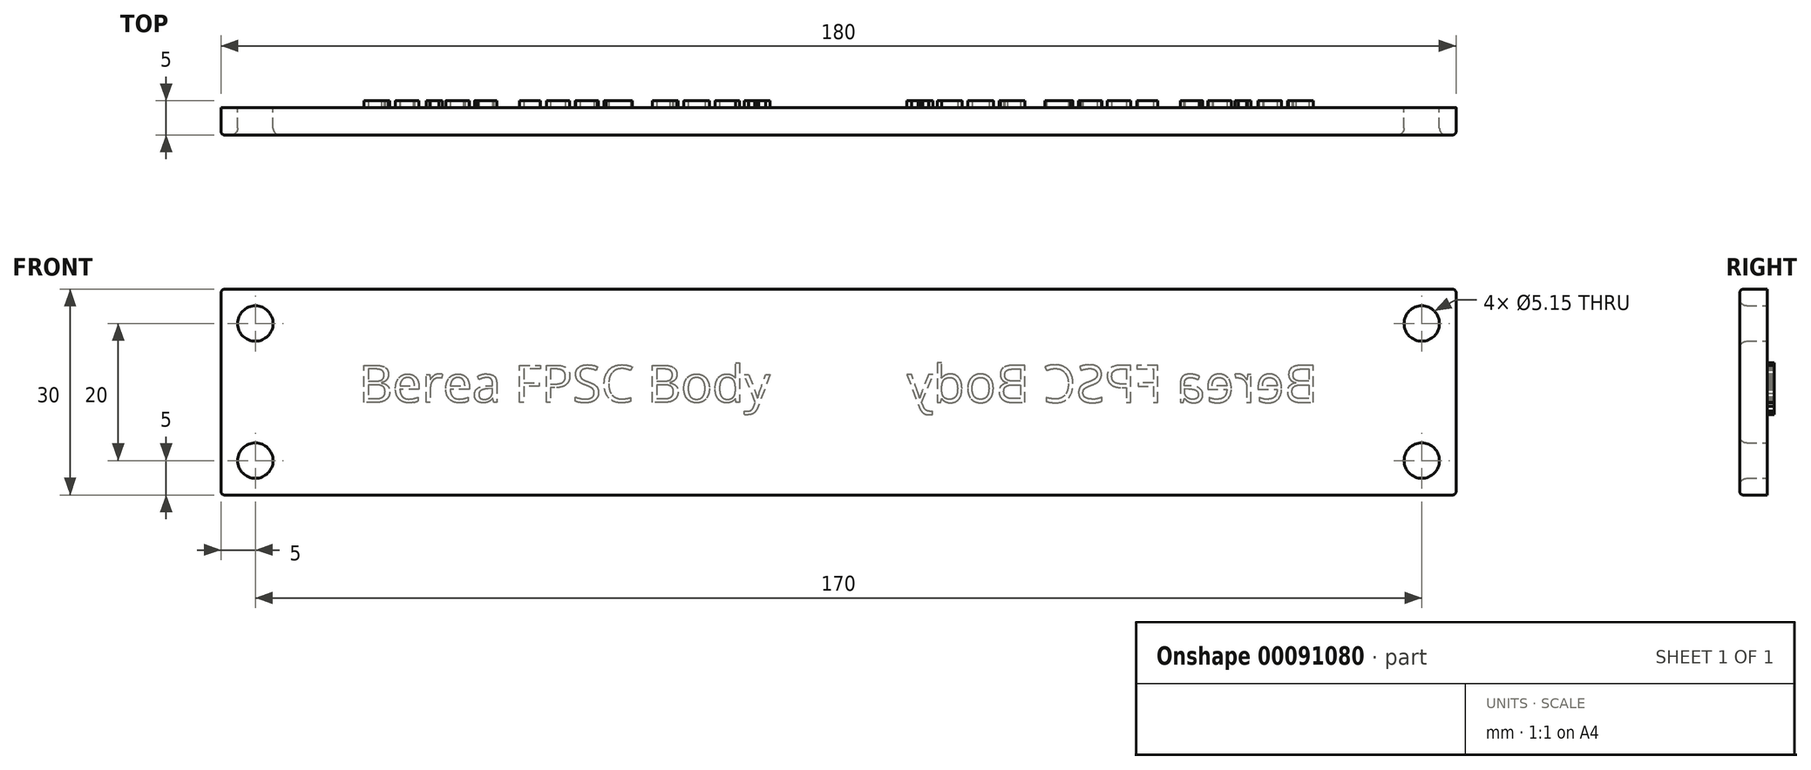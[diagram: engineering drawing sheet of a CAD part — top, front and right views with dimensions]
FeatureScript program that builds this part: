
annotation { "Feature Type Name" : "Feature", "Feature Type Description" : "" }
export const myFeature = defineFeature(function(context is Context, id is Id, definition is map)
    precondition{}
    {
        {
            var Q0;
            Q0=qCreatedBy(makeId("Front.planeOp"),FACE);
            var sketch = newSketch(context, id + "F0", { "sketchPlane" : qUnion([Q0])});
            skLineSegment(sketch, "E0.bottom", {"start": v(-90, -15) * mm, "end": v(90, -15) * mm});
            skLineSegment(sketch, "E0.top", {"start": v(-90, 15) * mm, "end": v(90, 15) * mm});
            skLineSegment(sketch, "E0.left", {"start": v(-90, -15) * mm, "end": v(-90, 15) * mm});
            skLineSegment(sketch, "E0.right", {"start": v(90, -15) * mm, "end": v(90, 15) * mm});
            skPoint(sketch, "E0.middle", {"position": v(0, 0) * mm});
            skCircle(sketch, "E1", {"center": v(-85, 10) * mm, "radius": 2.58 * mm});
            skPoint(sketch, "E2.start.orphan", {"position": v(-90, 0) * mm});
            skPoint(sketch, "E3.orphan", {"position": v(0, 15) * mm});
            skPoint(sketch, "E4.end.orphan", {"position": v(0, -15) * mm});
            skLineSegment(sketch, "E5", {"start": v(-90, 0) * mm, "end": v(0, 0) * mm, "construction": true});
            skLineSegment(sketch, "E6", {"start": v(0, 15) * mm, "end": v(0, -15) * mm, "construction": true});
            skCircle(sketch, "E7.MirrorC", {"center": v(-85, -10) * mm, "radius": 2.58 * mm});
            skCircle(sketch, "E8.MirrorC", {"center": v(85, 10) * mm, "radius": 2.58 * mm});
            skCircle(sketch, "E9.MirrorC", {"center": v(85, -10) * mm, "radius": 2.58 * mm});
            skSolve(sketch);
        }
        {
            var Q0;
            Q0=makeQuery(id+"F0.imprint","IMPRINT",FACE,{"disambiguationData":[TD([[makeQuery(id+"F0.imprint","IMPRINT",EDGE,{"derivedFrom":sQuery(id+"F0.wireOp",EDGE,"E0.bottom")}),1.0]])]});
            extrude(context, id + "F1", {"entities" : qUnion([Q0]), "depth" : 4 * mm});
        }
        {
            var Q0;
            Q0=makeQuery(id+"F1.opExtrude","CAP_EDGE",EDGE,{"disambiguationData":[OSD([sQuery(id+"F0.wireOp",EDGE,"E1")])],"isStart":false});
            var Q1;
            Q1=makeQuery(id+"F1.opExtrude","CAP_EDGE",EDGE,{"disambiguationData":[OSD([sQuery(id+"F0.wireOp",EDGE,"f5b72a5b-8583-449a-bdbf-9ac5a681e1fd0.MirrorC")])],"isStart":false});
            var Q2;
            Q2=makeQuery(id+"F1.opExtrude","CAP_EDGE",EDGE,{"disambiguationData":[OSD([sQuery(id+"F0.wireOp",EDGE,"2623e306-60f4-4522-aa65-1e3e8c2cf5b60.MirrorC")])],"isStart":false});
            var Q3;
            Q3=makeQuery(id+"F1.opExtrude","CAP_EDGE",EDGE,{"disambiguationData":[OSD([sQuery(id+"F0.wireOp",EDGE,"be81a34d-1d50-4ce7-a7a8-4484a1701fac0.MirrorC")])],"isStart":false});
            var Q4;
            Q4=makeQuery(id+"F1.opExtrude","CAP_EDGE",EDGE,{"disambiguationData":[OSD([sQuery(id+"F0.wireOp",EDGE,"E7.MirrorC")])],"isStart":false});
            var Q5;
            Q5=makeQuery(id+"F1.opExtrude","CAP_EDGE",EDGE,{"disambiguationData":[OSD([sQuery(id+"F0.wireOp",EDGE,"E8.MirrorC")])],"isStart":false});
            var Q6;
            Q6=makeQuery(id+"F1.opExtrude","CAP_EDGE",EDGE,{"disambiguationData":[OSD([sQuery(id+"F0.wireOp",EDGE,"E9.MirrorC")])],"isStart":false});
            fillet(context, id + "F2", {"entities" : qUnion([Q0, Q1, Q2, Q3, Q4, Q5, Q6]), "radius" : 1 * mm, "tangentPropagation" : true, "allowEdgeOverflow" : false});
        }
        {
            var Q0;
            Q0=makeQuery(id+"F1.opExtrude","CAP_EDGE",EDGE,{"disambiguationData":[OSD([sQuery(id+"F0.wireOp",EDGE,"E0.top")])],"isStart":false});
            var Q1;
            Q1=makeQuery(id+"F1.opExtrude","CAP_EDGE",EDGE,{"disambiguationData":[OSD([sQuery(id+"F0.wireOp",EDGE,"E0.left")])],"isStart":false});
            var Q2;
            Q2=makeQuery(id+"F1.opExtrude","CAP_EDGE",EDGE,{"disambiguationData":[OSD([sQuery(id+"F0.wireOp",EDGE,"E0.bottom")])],"isStart":false});
            var Q3;
            Q3=makeQuery(id+"F1.opExtrude","CAP_EDGE",EDGE,{"disambiguationData":[OSD([sQuery(id+"F0.wireOp",EDGE,"E0.right")])],"isStart":false});
            var Q4;
            Q4=makeQuery(id+"F1.opExtrude","SWEPT_EDGE",EDGE,{"disambiguationData":[OSD([sQuery(id+"F0.wireOp",EDGE,"E0.top"),sQuery(id+"F0.wireOp",EDGE,"E0.left")])]});
            var Q5;
            Q5=makeQuery(id+"F1.opExtrude","SWEPT_EDGE",EDGE,{"disambiguationData":[OSD([sQuery(id+"F0.wireOp",EDGE,"E0.bottom"),sQuery(id+"F0.wireOp",EDGE,"E0.left")])]});
            var Q6;
            Q6=makeQuery(id+"F1.opExtrude","SWEPT_EDGE",EDGE,{"disambiguationData":[OSD([sQuery(id+"F0.wireOp",EDGE,"E0.top"),sQuery(id+"F0.wireOp",EDGE,"E0.right")])]});
            var Q7;
            Q7=makeQuery(id+"F1.opExtrude","SWEPT_EDGE",EDGE,{"disambiguationData":[OSD([sQuery(id+"F0.wireOp",EDGE,"E0.bottom"),sQuery(id+"F0.wireOp",EDGE,"E0.right")])]});
            fillet(context, id + "F3", {"entities" : qUnion([Q0, Q1, Q2, Q3, Q4, Q5, Q6, Q7]), "radius" : .5 * mm, "tangentPropagation" : true, "allowEdgeOverflow" : false});
        }
        {
            var Q0;
            Q0=makeQuery(id+"F1.opExtrude","CAP_FACE",FACE,{"disambiguationData":[OSD([sQuery(id+"F0.wireOp",EDGE,"E0.bottom"),sQuery(id+"F0.wireOp",EDGE,"E0.top"),sQuery(id+"F0.wireOp",EDGE,"E0.left"),sQuery(id+"F0.wireOp",EDGE,"E0.right"),sQuery(id+"F0.wireOp",EDGE,"E1"),sQuery(id+"F0.wireOp",EDGE,"E7.MirrorC"),sQuery(id+"F0.wireOp",EDGE,"E8.MirrorC"),sQuery(id+"F0.wireOp",EDGE,"E9.MirrorC")])],"isStart":true});
            var sketch = newSketch(context, id + "F4", { "sketchPlane" : qUnion([Q0])});
            skText(sketch, "E10", { "text": "Berea FPSC Body", "fontName": "OpenSans-Regular.ttf"});
            skLineSegment(sketch, "E11", {"start": v(0, 15) * mm, "end": v(0, -15) * mm, "construction": true});
            const initialGuessF4  = {"E10": [-0.06991, -0.00149, 1, 0, 0.00545]};
            skSetInitialGuess(sketch, initialGuessF4);
            skSolve(sketch);
        }
        {
            var Q0;
            Q0=qSketchRegion(id+"F4",true);
            extrude(context, id + "F5", {"entities" : qUnion([Q0]), "operationType" : NewBodyOperationType.ADD, "depth" : 1 * mm});
        }
        {
            var Q0;
            Q0=makeQuery(id+"F1.opExtrude","SWEPT_BODY",BODY,{"disambiguationData":[OSD([sQuery(id+"F0.wireOp",EDGE,"E0.bottom"),sQuery(id+"F0.wireOp",EDGE,"E0.top"),sQuery(id+"F0.wireOp",EDGE,"E0.left"),sQuery(id+"F0.wireOp",EDGE,"E0.right"),sQuery(id+"F0.wireOp",EDGE,"E1"),sQuery(id+"F0.wireOp",EDGE,"E7.MirrorC"),sQuery(id+"F0.wireOp",EDGE,"E8.MirrorC"),sQuery(id+"F0.wireOp",EDGE,"E9.MirrorC")])]});
            var Q1;
            Q1=makeQuery(id+"F5.opExtrude","SWEPT_FACE",FACE,{"disambiguationData":[OSD([sQuery(id+"F4.wireOp",EDGE,"E10.sketch_text.stroke-94")])]});
            var Q2;
            Q2=makeQuery(id+"F5.opExtrude","SWEPT_FACE",FACE,{"disambiguationData":[OSD([sQuery(id+"F4.wireOp",EDGE,"E10.sketch_text.stroke-169")])]});
            var Q3;
            Q3=makeQuery(id+"F5.opExtrude","SWEPT_FACE",FACE,{"disambiguationData":[OSD([sQuery(id+"F4.wireOp",EDGE,"E10.sketch_text.stroke-185")])]});
            var Q4;
            Q4=makeQuery(id+"F5.opExtrude","SWEPT_FACE",FACE,{"disambiguationData":[OSD([sQuery(id+"F4.wireOp",EDGE,"E10.sketch_text.stroke-125")])]});
            var Q5;
            Q5=makeQuery(id+"F5.opExtrude","SWEPT_FACE",FACE,{"disambiguationData":[OSD([sQuery(id+"F4.wireOp",EDGE,"E10.sketch_text.stroke-155")])]});
            var Q6;
            Q6=makeQuery(id+"F5.opExtrude","SWEPT_FACE",FACE,{"disambiguationData":[OSD([sQuery(id+"F4.wireOp",EDGE,"E10.sketch_text.stroke-65")])]});
            var Q7;
            Q7=makeQuery(id+"F5.opExtrude","SWEPT_FACE",FACE,{"disambiguationData":[OSD([sQuery(id+"F4.wireOp",EDGE,"E10.sketch_text.stroke-81")])]});
            var Q8;
            Q8=makeQuery(id+"F5.opExtrude","SWEPT_FACE",FACE,{"disambiguationData":[OSD([sQuery(id+"F4.wireOp",EDGE,"E10.sketch_text.stroke-67")])]});
            var Q9;
            Q9=makeQuery(id+"F5.opExtrude","SWEPT_FACE",FACE,{"disambiguationData":[OSD([sQuery(id+"F4.wireOp",EDGE,"E10.sketch_text.stroke-99")])]});
            var Q10;
            Q10=makeQuery(id+"F5.opExtrude","SWEPT_FACE",FACE,{"disambiguationData":[OSD([sQuery(id+"F4.wireOp",EDGE,"E10.sketch_text.stroke-127")])]});
            var Q11;
            Q11=makeQuery(id+"F5.opExtrude","SWEPT_FACE",FACE,{"disambiguationData":[OSD([sQuery(id+"F4.wireOp",EDGE,"E10.sketch_text.stroke-10")])]});
            var Q12;
            Q12=makeQuery(id+"F5.opExtrude","CAP_FACE",FACE,{"disambiguationData":[OSD([sQuery(id+"F4.wireOp",EDGE,"E10.sketch_text.stroke-9"),sQuery(id+"F4.wireOp",EDGE,"E10.sketch_text.stroke-10"),sQuery(id+"F4.wireOp",EDGE,"E10.sketch_text.stroke-11"),sQuery(id+"F4.wireOp",EDGE,"E10.sketch_text.stroke-12")])],"isStart":false});
            var Q13;
            Q13=makeQuery(id+"F5.opExtrude","SWEPT_FACE",FACE,{"disambiguationData":[OSD([sQuery(id+"F4.wireOp",EDGE,"E10.sketch_text.stroke-154")])]});
            var Q14;
            Q14=makeQuery(id+"F5.opExtrude","SWEPT_FACE",FACE,{"disambiguationData":[OSD([sQuery(id+"F4.wireOp",EDGE,"E10.sketch_text.stroke-1")])]});
            var Q15;
            Q15=makeQuery(id+"F5.opExtrude","CAP_FACE",FACE,{"disambiguationData":[OSD([sQuery(id+"F4.wireOp",EDGE,"E10.sketch_text.stroke-124"),sQuery(id+"F4.wireOp",EDGE,"E10.sketch_text.stroke-125"),sQuery(id+"F4.wireOp",EDGE,"E10.sketch_text.stroke-126"),sQuery(id+"F4.wireOp",EDGE,"E10.sketch_text.stroke-127"),sQuery(id+"F4.wireOp",EDGE,"E10.sketch_text.stroke-128"),sQuery(id+"F4.wireOp",EDGE,"E10.sketch_text.stroke-129"),sQuery(id+"F4.wireOp",EDGE,"E10.sketch_text.stroke-130"),sQuery(id+"F4.wireOp",EDGE,"E10.sketch_text.stroke-131"),sQuery(id+"F4.wireOp",EDGE,"E10.sketch_text.stroke-132"),sQuery(id+"F4.wireOp",EDGE,"E10.sketch_text.stroke-133"),sQuery(id+"F4.wireOp",EDGE,"E10.sketch_text.stroke-134"),sQuery(id+"F4.wireOp",EDGE,"E10.sketch_text.stroke-135"),sQuery(id+"F4.wireOp",EDGE,"E10.sketch_text.stroke-136"),sQuery(id+"F4.wireOp",EDGE,"E10.sketch_text.stroke-137"),sQuery(id+"F4.wireOp",EDGE,"E10.sketch_text.stroke-138")])],"isStart":false});
            var Q16;
            Q16=makeQuery(id+"F5.opExtrude","CAP_FACE",FACE,{"disambiguationData":[OSD([sQuery(id+"F4.wireOp",EDGE,"E10.sketch_text.stroke-34"),sQuery(id+"F4.wireOp",EDGE,"E10.sketch_text.stroke-35"),sQuery(id+"F4.wireOp",EDGE,"E10.sketch_text.stroke-36"),sQuery(id+"F4.wireOp",EDGE,"E10.sketch_text.stroke-37"),sQuery(id+"F4.wireOp",EDGE,"E10.sketch_text.stroke-38"),sQuery(id+"F4.wireOp",EDGE,"E10.sketch_text.stroke-39"),sQuery(id+"F4.wireOp",EDGE,"E10.sketch_text.stroke-40"),sQuery(id+"F4.wireOp",EDGE,"E10.sketch_text.stroke-41"),sQuery(id+"F4.wireOp",EDGE,"E10.sketch_text.stroke-42"),sQuery(id+"F4.wireOp",EDGE,"E10.sketch_text.stroke-43"),sQuery(id+"F4.wireOp",EDGE,"E10.sketch_text.stroke-44"),sQuery(id+"F4.wireOp",EDGE,"E10.sketch_text.stroke-45"),sQuery(id+"F4.wireOp",EDGE,"E10.sketch_text.stroke-46"),sQuery(id+"F4.wireOp",EDGE,"E10.sketch_text.stroke-47"),sQuery(id+"F4.wireOp",EDGE,"E10.sketch_text.stroke-48"),sQuery(id+"F4.wireOp",EDGE,"E10.sketch_text.stroke-49"),sQuery(id+"F4.wireOp",EDGE,"E10.sketch_text.stroke-50"),sQuery(id+"F4.wireOp",EDGE,"E10.sketch_text.stroke-51"),sQuery(id+"F4.wireOp",EDGE,"E10.sketch_text.stroke-52"),sQuery(id+"F4.wireOp",EDGE,"E10.sketch_text.stroke-53"),sQuery(id+"F4.wireOp",EDGE,"E10.sketch_text.stroke-54"),sQuery(id+"F4.wireOp",EDGE,"E10.sketch_text.stroke-55"),sQuery(id+"F4.wireOp",EDGE,"E10.sketch_text.stroke-56"),sQuery(id+"F4.wireOp",EDGE,"E10.sketch_text.stroke-57"),sQuery(id+"F4.wireOp",EDGE,"E10.sketch_text.stroke-58"),sQuery(id+"F4.wireOp",EDGE,"E10.sketch_text.stroke-59"),sQuery(id+"F4.wireOp",EDGE,"E10.sketch_text.stroke-60")])],"isStart":false});
            var Q17;
            Q17=makeQuery(id+"F5.opExtrude","SWEPT_FACE",FACE,{"disambiguationData":[OSD([sQuery(id+"F4.wireOp",EDGE,"E10.sketch_text.stroke-50")])]});
            var Q18;
            Q18=makeQuery(id+"F5.opExtrude","SWEPT_FACE",FACE,{"disambiguationData":[OSD([sQuery(id+"F4.wireOp",EDGE,"E10.sketch_text.stroke-2")])]});
            var Q19;
            Q19=makeQuery(id+"F5.opExtrude","SWEPT_FACE",FACE,{"disambiguationData":[OSD([sQuery(id+"F4.wireOp",EDGE,"E10.sketch_text.stroke-3")])]});
            var Q20;
            Q20=makeQuery(id+"F5.opExtrude","SWEPT_FACE",FACE,{"disambiguationData":[OSD([sQuery(id+"F4.wireOp",EDGE,"E10.sketch_text.stroke-5")])]});
            var Q21;
            Q21=makeQuery(id+"F5.opExtrude","SWEPT_FACE",FACE,{"disambiguationData":[OSD([sQuery(id+"F4.wireOp",EDGE,"E10.sketch_text.stroke-8")])]});
            var Q22;
            Q22=makeQuery(id+"F5.opExtrude","SWEPT_FACE",FACE,{"disambiguationData":[OSD([sQuery(id+"F4.wireOp",EDGE,"E10.sketch_text.stroke-98")])]});
            var Q23;
            Q23=makeQuery(id+"F5.opExtrude","SWEPT_FACE",FACE,{"disambiguationData":[OSD([sQuery(id+"F4.wireOp",EDGE,"E10.sketch_text.stroke-66")])]});
            var Q24;
            Q24=makeQuery(id+"F5.opExtrude","SWEPT_FACE",FACE,{"disambiguationData":[OSD([sQuery(id+"F4.wireOp",EDGE,"E10.sketch_text.stroke-153")])]});
            var Q25;
            Q25=makeQuery(id+"F5.opExtrude","SWEPT_FACE",FACE,{"disambiguationData":[OSD([sQuery(id+"F4.wireOp",EDGE,"E10.sketch_text.stroke-126")])]});
            var Q26;
            Q26=makeQuery(id+"F5.opExtrude","SWEPT_FACE",FACE,{"disambiguationData":[OSD([sQuery(id+"F4.wireOp",EDGE,"E10.sketch_text.stroke-183")])]});
            var Q27;
            Q27=makeQuery(id+"F5.opExtrude","SWEPT_FACE",FACE,{"disambiguationData":[OSD([sQuery(id+"F4.wireOp",EDGE,"E10.sketch_text.stroke-109")])]});
            var Q28;
            Q28=makeQuery(id+"F5.opExtrude","SWEPT_FACE",FACE,{"disambiguationData":[OSD([sQuery(id+"F4.wireOp",EDGE,"E10.sketch_text.stroke-186")])]});
            var Q29;
            Q29=makeQuery(id+"F5.opExtrude","SWEPT_FACE",FACE,{"disambiguationData":[OSD([sQuery(id+"F4.wireOp",EDGE,"E10.sketch_text.stroke-79")])]});
            var Q30;
            Q30=makeQuery(id+"F5.opExtrude","SWEPT_FACE",FACE,{"disambiguationData":[OSD([sQuery(id+"F4.wireOp",EDGE,"E10.sketch_text.stroke-110")])]});
            var Q31;
            Q31=makeQuery(id+"F5.opExtrude","SWEPT_FACE",FACE,{"disambiguationData":[OSD([sQuery(id+"F4.wireOp",EDGE,"E10.sketch_text.stroke-38")])]});
            var Q32;
            Q32=makeQuery(id+"F5.opExtrude","SWEPT_FACE",FACE,{"disambiguationData":[OSD([sQuery(id+"F4.wireOp",EDGE,"E10.sketch_text.stroke-24")])]});
            var Q33;
            Q33=makeQuery(id+"F5.opExtrude","SWEPT_FACE",FACE,{"disambiguationData":[OSD([sQuery(id+"F4.wireOp",EDGE,"E10.sketch_text.stroke-12")])]});
            var Q34;
            Q34=makeQuery(id+"F5.opExtrude","SWEPT_FACE",FACE,{"disambiguationData":[OSD([sQuery(id+"F4.wireOp",EDGE,"E10.sketch_text.stroke-100")])]});
            var Q35;
            Q35=makeQuery(id+"F5.opExtrude","SWEPT_FACE",FACE,{"disambiguationData":[OSD([sQuery(id+"F4.wireOp",EDGE,"E10.sketch_text.stroke-158")])]});
            var Q36;
            Q36=makeQuery(id+"F5.opExtrude","SWEPT_FACE",FACE,{"disambiguationData":[OSD([sQuery(id+"F4.wireOp",EDGE,"E10.sketch_text.stroke-142")])]});
            var Q37;
            Q37=makeQuery(id+"F5.opExtrude","SWEPT_FACE",FACE,{"disambiguationData":[OSD([sQuery(id+"F4.wireOp",EDGE,"E10.sketch_text.stroke-54")])]});
            var Q38;
            Q38=makeQuery(id+"F5.opExtrude","SWEPT_FACE",FACE,{"disambiguationData":[OSD([sQuery(id+"F4.wireOp",EDGE,"E10.sketch_text.stroke-25")])]});
            var Q39;
            Q39=makeQuery(id+"F5.opExtrude","SWEPT_FACE",FACE,{"disambiguationData":[OSD([sQuery(id+"F4.wireOp",EDGE,"E10.sketch_text.stroke-101")])]});
            var Q40;
            Q40=makeQuery(id+"F5.opExtrude","SWEPT_FACE",FACE,{"disambiguationData":[OSD([sQuery(id+"F4.wireOp",EDGE,"E10.sketch_text.stroke-69")])]});
            var Q41;
            Q41=makeQuery(id+"F5.opExtrude","SWEPT_FACE",FACE,{"disambiguationData":[OSD([sQuery(id+"F4.wireOp",EDGE,"E10.sketch_text.stroke-159")])]});
            var Q42;
            Q42=makeQuery(id+"F5.opExtrude","SWEPT_FACE",FACE,{"disambiguationData":[OSD([sQuery(id+"F4.wireOp",EDGE,"E10.sketch_text.stroke-85")])]});
            var Q43;
            Q43=makeQuery(id+"F5.opExtrude","SWEPT_FACE",FACE,{"disambiguationData":[OSD([sQuery(id+"F4.wireOp",EDGE,"E10.sketch_text.stroke-173")])]});
            var Q44;
            Q44=makeQuery(id+"F5.opExtrude","SWEPT_FACE",FACE,{"disambiguationData":[OSD([sQuery(id+"F4.wireOp",EDGE,"E10.sketch_text.stroke-40")])]});
            var Q45;
            Q45=makeQuery(id+"F5.opExtrude","SWEPT_FACE",FACE,{"disambiguationData":[OSD([sQuery(id+"F4.wireOp",EDGE,"E10.sketch_text.stroke-102")])]});
            var Q46;
            Q46=makeQuery(id+"F5.opExtrude","SWEPT_FACE",FACE,{"disambiguationData":[OSD([sQuery(id+"F4.wireOp",EDGE,"E10.sketch_text.stroke-86")])]});
            var Q47;
            Q47=makeQuery(id+"F5.opExtrude","SWEPT_FACE",FACE,{"disambiguationData":[OSD([sQuery(id+"F4.wireOp",EDGE,"E10.sketch_text.stroke-130")])]});
            var Q48;
            Q48=makeQuery(id+"F5.opExtrude","SWEPT_FACE",FACE,{"disambiguationData":[OSD([sQuery(id+"F4.wireOp",EDGE,"E10.sketch_text.stroke-103")])]});
            var Q49;
            Q49=makeQuery(id+"F5.opExtrude","SWEPT_FACE",FACE,{"disambiguationData":[OSD([sQuery(id+"F4.wireOp",EDGE,"E10.sketch_text.stroke-87")])]});
            var Q50;
            Q50=makeQuery(id+"F5.opExtrude","SWEPT_FACE",FACE,{"disambiguationData":[OSD([sQuery(id+"F4.wireOp",EDGE,"E10.sketch_text.stroke-145")])]});
            var Q51;
            Q51=makeQuery(id+"F5.opExtrude","SWEPT_FACE",FACE,{"disambiguationData":[OSD([sQuery(id+"F4.wireOp",EDGE,"E10.sketch_text.stroke-131")])]});
            var Q52;
            Q52=makeQuery(id+"F5.opExtrude","SWEPT_FACE",FACE,{"disambiguationData":[OSD([sQuery(id+"F4.wireOp",EDGE,"E10.sketch_text.stroke-28")])]});
            var Q53;
            Q53=makeQuery(id+"F5.opExtrude","SWEPT_FACE",FACE,{"disambiguationData":[OSD([sQuery(id+"F4.wireOp",EDGE,"E10.sketch_text.stroke-14")])]});
            var Q54;
            Q54=makeQuery(id+"F5.opExtrude","SWEPT_FACE",FACE,{"disambiguationData":[OSD([sQuery(id+"F4.wireOp",EDGE,"E10.sketch_text.stroke-88")])]});
            var Q55;
            Q55=makeQuery(id+"F5.opExtrude","SWEPT_FACE",FACE,{"disambiguationData":[OSD([sQuery(id+"F4.wireOp",EDGE,"E10.sketch_text.stroke-162")])]});
            var Q56;
            Q56=makeQuery(id+"F5.opExtrude","SWEPT_FACE",FACE,{"disambiguationData":[OSD([sQuery(id+"F4.wireOp",EDGE,"E10.sketch_text.stroke-176")])]});
            var Q57;
            Q57=makeQuery(id+"F5.opExtrude","SWEPT_FACE",FACE,{"disambiguationData":[OSD([sQuery(id+"F4.wireOp",EDGE,"E10.sketch_text.stroke-73")])]});
            var Q58;
            Q58=makeQuery(id+"F5.opExtrude","SWEPT_FACE",FACE,{"disambiguationData":[OSD([sQuery(id+"F4.wireOp",EDGE,"E10.sketch_text.stroke-59")])]});
            var Q59;
            Q59=makeQuery(id+"F5.opExtrude","SWEPT_FACE",FACE,{"disambiguationData":[OSD([sQuery(id+"F4.wireOp",EDGE,"E10.sketch_text.stroke-133")])]});
            var Q60;
            Q60=makeQuery(id+"F5.opExtrude","SWEPT_FACE",FACE,{"disambiguationData":[OSD([sQuery(id+"F4.wireOp",EDGE,"E10.sketch_text.stroke-119")])]});
            var Q61;
            Q61=makeQuery(id+"F5.opExtrude","SWEPT_FACE",FACE,{"disambiguationData":[OSD([sQuery(id+"F4.wireOp",EDGE,"E10.sketch_text.stroke-74")])]});
            var Q62;
            Q62=makeQuery(id+"F5.opExtrude","SWEPT_FACE",FACE,{"disambiguationData":[OSD([sQuery(id+"F4.wireOp",EDGE,"E10.sketch_text.stroke-44")])]});
            var Q63;
            Q63=makeQuery(id+"F5.opExtrude","SWEPT_FACE",FACE,{"disambiguationData":[OSD([sQuery(id+"F4.wireOp",EDGE,"E10.sketch_text.stroke-120")])]});
            var Q64;
            Q64=makeQuery(id+"F5.opExtrude","SWEPT_FACE",FACE,{"disambiguationData":[OSD([sQuery(id+"F4.wireOp",EDGE,"E10.sketch_text.stroke-90")])]});
            var Q65;
            Q65=makeQuery(id+"F5.opExtrude","SWEPT_FACE",FACE,{"disambiguationData":[OSD([sQuery(id+"F4.wireOp",EDGE,"E10.sketch_text.stroke-178")])]});
            var Q66;
            Q66=makeQuery(id+"F5.opExtrude","SWEPT_FACE",FACE,{"disambiguationData":[OSD([sQuery(id+"F4.wireOp",EDGE,"E10.sketch_text.stroke-45")])]});
            var Q67;
            Q67=makeQuery(id+"F5.opExtrude","SWEPT_FACE",FACE,{"disambiguationData":[OSD([sQuery(id+"F4.wireOp",EDGE,"E10.sketch_text.stroke-31")])]});
            var Q68;
            Q68=makeQuery(id+"F5.opExtrude","SWEPT_FACE",FACE,{"disambiguationData":[OSD([sQuery(id+"F4.wireOp",EDGE,"E10.sketch_text.stroke-135")])]});
            var Q69;
            Q69=makeQuery(id+"F5.opExtrude","SWEPT_FACE",FACE,{"disambiguationData":[OSD([sQuery(id+"F4.wireOp",EDGE,"E10.sketch_text.stroke-179")])]});
            var Q70;
            Q70=makeQuery(id+"F5.opExtrude","SWEPT_FACE",FACE,{"disambiguationData":[OSD([sQuery(id+"F4.wireOp",EDGE,"E10.sketch_text.stroke-165")])]});
            var Q71;
            Q71=makeQuery(id+"F5.opExtrude","SWEPT_FACE",FACE,{"disambiguationData":[OSD([sQuery(id+"F4.wireOp",EDGE,"E10.sketch_text.stroke-149")])]});
            var Q72;
            Q72=makeQuery(id+"F5.opExtrude","SWEPT_FACE",FACE,{"disambiguationData":[OSD([sQuery(id+"F4.wireOp",EDGE,"E10.sketch_text.stroke-136")])]});
            var Q73;
            Q73=makeQuery(id+"F5.opExtrude","SWEPT_FACE",FACE,{"disambiguationData":[OSD([sQuery(id+"F4.wireOp",EDGE,"E10.sketch_text.stroke-122")])]});
            var Q74;
            Q74=makeQuery(id+"F5.opExtrude","SWEPT_FACE",FACE,{"disambiguationData":[OSD([sQuery(id+"F4.wireOp",EDGE,"E10.sketch_text.stroke-106")])]});
            var Q75;
            Q75=makeQuery(id+"F5.opExtrude","SWEPT_FACE",FACE,{"disambiguationData":[OSD([sQuery(id+"F4.wireOp",EDGE,"E10.sketch_text.stroke-180")])]});
            var Q76;
            Q76=makeQuery(id+"F5.opExtrude","SWEPT_FACE",FACE,{"disambiguationData":[OSD([sQuery(id+"F4.wireOp",EDGE,"E10.sketch_text.stroke-166")])]});
            var Q77;
            Q77=makeQuery(id+"F5.opExtrude","SWEPT_FACE",FACE,{"disambiguationData":[OSD([sQuery(id+"F4.wireOp",EDGE,"E10.sketch_text.stroke-150")])]});
            var Q78;
            Q78=makeQuery(id+"F5.opExtrude","SWEPT_FACE",FACE,{"disambiguationData":[OSD([sQuery(id+"F4.wireOp",EDGE,"E10.sketch_text.stroke-76")])]});
            var Q79;
            Q79=makeQuery(id+"F5.opExtrude","SWEPT_FACE",FACE,{"disambiguationData":[OSD([sQuery(id+"F4.wireOp",EDGE,"E10.sketch_text.stroke-32")])]});
            var Q80;
            Q80=makeQuery(id+"F5.opExtrude","SWEPT_FACE",FACE,{"disambiguationData":[OSD([sQuery(id+"F4.wireOp",EDGE,"E10.sketch_text.stroke-181")])]});
            var Q81;
            Q81=makeQuery(id+"F5.opExtrude","SWEPT_FACE",FACE,{"disambiguationData":[OSD([sQuery(id+"F4.wireOp",EDGE,"E10.sketch_text.stroke-47")])]});
            var Q82;
            Q82=makeQuery(id+"F5.opExtrude","SWEPT_FACE",FACE,{"disambiguationData":[OSD([sQuery(id+"F4.wireOp",EDGE,"E10.sketch_text.stroke-123")])]});
            var Q83;
            Q83=makeQuery(id+"F5.opExtrude","SWEPT_FACE",FACE,{"disambiguationData":[OSD([sQuery(id+"F4.wireOp",EDGE,"E10.sketch_text.stroke-107")])]});
            var Q84;
            Q84=makeQuery(id+"F5.opExtrude","SWEPT_FACE",FACE,{"disambiguationData":[OSD([sQuery(id+"F4.wireOp",EDGE,"E10.sketch_text.stroke-48")])]});
            var Q85;
            Q85=makeQuery(id+"F5.opExtrude","SWEPT_FACE",FACE,{"disambiguationData":[OSD([sQuery(id+"F4.wireOp",EDGE,"E10.sketch_text.stroke-124")])]});
            var Q86;
            Q86=makeQuery(id+"F5.opExtrude","SWEPT_FACE",FACE,{"disambiguationData":[OSD([sQuery(id+"F4.wireOp",EDGE,"E10.sketch_text.stroke-108")])]});
            var Q87;
            Q87=makeQuery(id+"F5.opExtrude","CAP_FACE",FACE,{"disambiguationData":[OSD([sQuery(id+"F4.wireOp",EDGE,"E10.sketch_text.stroke-139"),sQuery(id+"F4.wireOp",EDGE,"E10.sketch_text.stroke-140"),sQuery(id+"F4.wireOp",EDGE,"E10.sketch_text.stroke-141"),sQuery(id+"F4.wireOp",EDGE,"E10.sketch_text.stroke-142"),sQuery(id+"F4.wireOp",EDGE,"E10.sketch_text.stroke-143"),sQuery(id+"F4.wireOp",EDGE,"E10.sketch_text.stroke-144"),sQuery(id+"F4.wireOp",EDGE,"E10.sketch_text.stroke-145"),sQuery(id+"F4.wireOp",EDGE,"E10.sketch_text.stroke-146"),sQuery(id+"F4.wireOp",EDGE,"E10.sketch_text.stroke-147"),sQuery(id+"F4.wireOp",EDGE,"E10.sketch_text.stroke-148"),sQuery(id+"F4.wireOp",EDGE,"E10.sketch_text.stroke-149"),sQuery(id+"F4.wireOp",EDGE,"E10.sketch_text.stroke-150"),sQuery(id+"F4.wireOp",EDGE,"E10.sketch_text.stroke-151"),sQuery(id+"F4.wireOp",EDGE,"E10.sketch_text.stroke-152"),sQuery(id+"F4.wireOp",EDGE,"E10.sketch_text.stroke-153"),sQuery(id+"F4.wireOp",EDGE,"E10.sketch_text.stroke-154"),sQuery(id+"F4.wireOp",EDGE,"E10.sketch_text.stroke-155"),sQuery(id+"F4.wireOp",EDGE,"E10.sketch_text.stroke-156"),sQuery(id+"F4.wireOp",EDGE,"E10.sketch_text.stroke-157"),sQuery(id+"F4.wireOp",EDGE,"E10.sketch_text.stroke-158"),sQuery(id+"F4.wireOp",EDGE,"E10.sketch_text.stroke-159"),sQuery(id+"F4.wireOp",EDGE,"E10.sketch_text.stroke-160"),sQuery(id+"F4.wireOp",EDGE,"E10.sketch_text.stroke-161"),sQuery(id+"F4.wireOp",EDGE,"E10.sketch_text.stroke-162"),sQuery(id+"F4.wireOp",EDGE,"E10.sketch_text.stroke-163"),sQuery(id+"F4.wireOp",EDGE,"E10.sketch_text.stroke-164"),sQuery(id+"F4.wireOp",EDGE,"E10.sketch_text.stroke-165")])],"isStart":false});
            var Q88;
            Q88=makeQuery(id+"F5.opExtrude","CAP_FACE",FACE,{"disambiguationData":[OSD([sQuery(id+"F4.wireOp",EDGE,"E10.sketch_text.stroke-21"),sQuery(id+"F4.wireOp",EDGE,"E10.sketch_text.stroke-22"),sQuery(id+"F4.wireOp",EDGE,"E10.sketch_text.stroke-23"),sQuery(id+"F4.wireOp",EDGE,"E10.sketch_text.stroke-24"),sQuery(id+"F4.wireOp",EDGE,"E10.sketch_text.stroke-25"),sQuery(id+"F4.wireOp",EDGE,"E10.sketch_text.stroke-26"),sQuery(id+"F4.wireOp",EDGE,"E10.sketch_text.stroke-27"),sQuery(id+"F4.wireOp",EDGE,"E10.sketch_text.stroke-28"),sQuery(id+"F4.wireOp",EDGE,"E10.sketch_text.stroke-29"),sQuery(id+"F4.wireOp",EDGE,"E10.sketch_text.stroke-30"),sQuery(id+"F4.wireOp",EDGE,"E10.sketch_text.stroke-31"),sQuery(id+"F4.wireOp",EDGE,"E10.sketch_text.stroke-32"),sQuery(id+"F4.wireOp",EDGE,"E10.sketch_text.stroke-33")])],"isStart":false});
            var Q89;
            Q89=makeQuery(id+"F5.opExtrude","SWEPT_FACE",FACE,{"disambiguationData":[OSD([sQuery(id+"F4.wireOp",EDGE,"E10.sketch_text.stroke-113")])]});
            var Q90;
            Q90=makeQuery(id+"F5.opExtrude","SWEPT_FACE",FACE,{"disambiguationData":[OSD([sQuery(id+"F4.wireOp",EDGE,"E10.sketch_text.stroke-37")])]});
            var Q91;
            Q91=makeQuery(id+"F5.opExtrude","SWEPT_FACE",FACE,{"disambiguationData":[OSD([sQuery(id+"F4.wireOp",EDGE,"E10.sketch_text.stroke-187")])]});
            var Q92;
            Q92=makeQuery(id+"F5.opExtrude","SWEPT_FACE",FACE,{"disambiguationData":[OSD([sQuery(id+"F4.wireOp",EDGE,"E10.sketch_text.stroke-0")])]});
            var Q93;
            Q93=makeQuery(id+"F5.opExtrude","SWEPT_FACE",FACE,{"disambiguationData":[OSD([sQuery(id+"F4.wireOp",EDGE,"E10.sketch_text.stroke-4")])]});
            var Q94;
            Q94=makeQuery(id+"F5.opExtrude","SWEPT_FACE",FACE,{"disambiguationData":[OSD([sQuery(id+"F4.wireOp",EDGE,"E10.sketch_text.stroke-82")])]});
            var Q95;
            Q95=makeQuery(id+"F5.opExtrude","SWEPT_FACE",FACE,{"disambiguationData":[OSD([sQuery(id+"F4.wireOp",EDGE,"E10.sketch_text.stroke-52")])]});
            var Q96;
            Q96=makeQuery(id+"F5.opExtrude","SWEPT_FACE",FACE,{"disambiguationData":[OSD([sQuery(id+"F4.wireOp",EDGE,"E10.sketch_text.stroke-49")])]});
            var Q97;
            Q97=makeQuery(id+"F5.opExtrude","SWEPT_FACE",FACE,{"disambiguationData":[OSD([sQuery(id+"F4.wireOp",EDGE,"E10.sketch_text.stroke-63")])]});
            var Q98;
            Q98=makeQuery(id+"F5.opExtrude","SWEPT_FACE",FACE,{"disambiguationData":[OSD([sQuery(id+"F4.wireOp",EDGE,"E10.sketch_text.stroke-21")])]});
            var Q99;
            Q99=makeQuery(id+"F5.opExtrude","SWEPT_FACE",FACE,{"disambiguationData":[OSD([sQuery(id+"F4.wireOp",EDGE,"E10.sketch_text.stroke-128")])]});
            var Q100;
            Q100=makeQuery(id+"F5.opExtrude","SWEPT_FACE",FACE,{"disambiguationData":[OSD([sQuery(id+"F4.wireOp",EDGE,"E10.sketch_text.stroke-55")])]});
            var Q101;
            Q101=makeQuery(id+"F5.opExtrude","SWEPT_FACE",FACE,{"disambiguationData":[OSD([sQuery(id+"F4.wireOp",EDGE,"E10.sketch_text.stroke-26")])]});
            var Q102;
            Q102=makeQuery(id+"F5.opExtrude","SWEPT_FACE",FACE,{"disambiguationData":[OSD([sQuery(id+"F4.wireOp",EDGE,"E10.sketch_text.stroke-174")])]});
            var Q103;
            Q103=makeQuery(id+"F5.opExtrude","SWEPT_FACE",FACE,{"disambiguationData":[OSD([sQuery(id+"F4.wireOp",EDGE,"E10.sketch_text.stroke-104")])]});
            var Q104;
            Q104=makeQuery(id+"F5.opExtrude","SWEPT_FACE",FACE,{"disambiguationData":[OSD([sQuery(id+"F4.wireOp",EDGE,"E10.sketch_text.stroke-72")])]});
            var Q105;
            Q105=makeQuery(id+"F5.opExtrude","SWEPT_FACE",FACE,{"disambiguationData":[OSD([sQuery(id+"F4.wireOp",EDGE,"E10.sketch_text.stroke-132")])]});
            var Q106;
            Q106=makeQuery(id+"F5.opExtrude","SWEPT_FACE",FACE,{"disambiguationData":[OSD([sQuery(id+"F4.wireOp",EDGE,"E10.sketch_text.stroke-43")])]});
            var Q107;
            Q107=makeQuery(id+"F5.opExtrude","SWEPT_FACE",FACE,{"disambiguationData":[OSD([sQuery(id+"F4.wireOp",EDGE,"E10.sketch_text.stroke-15")])]});
            var Q108;
            Q108=makeQuery(id+"F5.opExtrude","SWEPT_FACE",FACE,{"disambiguationData":[OSD([sQuery(id+"F4.wireOp",EDGE,"E10.sketch_text.stroke-89")])]});
            var Q109;
            Q109=makeQuery(id+"F5.opExtrude","SWEPT_FACE",FACE,{"disambiguationData":[OSD([sQuery(id+"F4.wireOp",EDGE,"E10.sketch_text.stroke-163")])]});
            var Q110;
            Q110=makeQuery(id+"F5.opExtrude","SWEPT_FACE",FACE,{"disambiguationData":[OSD([sQuery(id+"F4.wireOp",EDGE,"E10.sketch_text.stroke-30")])]});
            var Q111;
            Q111=makeQuery(id+"F5.opExtrude","SWEPT_FACE",FACE,{"disambiguationData":[OSD([sQuery(id+"F4.wireOp",EDGE,"E10.sketch_text.stroke-134")])]});
            var Q112;
            Q112=makeQuery(id+"F5.opExtrude","SWEPT_FACE",FACE,{"disambiguationData":[OSD([sQuery(id+"F4.wireOp",EDGE,"E10.sketch_text.stroke-121")])]});
            var Q113;
            Q113=makeQuery(id+"F5.opExtrude","CAP_FACE",FACE,{"disambiguationData":[OSD([sQuery(id+"F4.wireOp",EDGE,"E10.sketch_text.stroke-105"),sQuery(id+"F4.wireOp",EDGE,"E10.sketch_text.stroke-106"),sQuery(id+"F4.wireOp",EDGE,"E10.sketch_text.stroke-107"),sQuery(id+"F4.wireOp",EDGE,"E10.sketch_text.stroke-108"),sQuery(id+"F4.wireOp",EDGE,"E10.sketch_text.stroke-109"),sQuery(id+"F4.wireOp",EDGE,"E10.sketch_text.stroke-110"),sQuery(id+"F4.wireOp",EDGE,"E10.sketch_text.stroke-111"),sQuery(id+"F4.wireOp",EDGE,"E10.sketch_text.stroke-112"),sQuery(id+"F4.wireOp",EDGE,"E10.sketch_text.stroke-113"),sQuery(id+"F4.wireOp",EDGE,"E10.sketch_text.stroke-114"),sQuery(id+"F4.wireOp",EDGE,"E10.sketch_text.stroke-115"),sQuery(id+"F4.wireOp",EDGE,"E10.sketch_text.stroke-116"),sQuery(id+"F4.wireOp",EDGE,"E10.sketch_text.stroke-117"),sQuery(id+"F4.wireOp",EDGE,"E10.sketch_text.stroke-118"),sQuery(id+"F4.wireOp",EDGE,"E10.sketch_text.stroke-119"),sQuery(id+"F4.wireOp",EDGE,"E10.sketch_text.stroke-120"),sQuery(id+"F4.wireOp",EDGE,"E10.sketch_text.stroke-121"),sQuery(id+"F4.wireOp",EDGE,"E10.sketch_text.stroke-122"),sQuery(id+"F4.wireOp",EDGE,"E10.sketch_text.stroke-123")])],"isStart":false});
            var Q114;
            Q114=makeQuery(id+"F5.opExtrude","SWEPT_FACE",FACE,{"disambiguationData":[OSD([sQuery(id+"F4.wireOp",EDGE,"E10.sketch_text.stroke-92")])]});
            var Q115;
            Q115=makeQuery(id+"F5.opExtrude","SWEPT_FACE",FACE,{"disambiguationData":[OSD([sQuery(id+"F4.wireOp",EDGE,"E10.sketch_text.stroke-46")])]});
            var Q116;
            Q116=makeQuery(id+"F5.opExtrude","CAP_FACE",FACE,{"disambiguationData":[OSD([sQuery(id+"F4.wireOp",EDGE,"E10.sketch_text.stroke-61"),sQuery(id+"F4.wireOp",EDGE,"E10.sketch_text.stroke-62"),sQuery(id+"F4.wireOp",EDGE,"E10.sketch_text.stroke-63"),sQuery(id+"F4.wireOp",EDGE,"E10.sketch_text.stroke-64"),sQuery(id+"F4.wireOp",EDGE,"E10.sketch_text.stroke-65"),sQuery(id+"F4.wireOp",EDGE,"E10.sketch_text.stroke-66"),sQuery(id+"F4.wireOp",EDGE,"E10.sketch_text.stroke-67"),sQuery(id+"F4.wireOp",EDGE,"E10.sketch_text.stroke-68"),sQuery(id+"F4.wireOp",EDGE,"E10.sketch_text.stroke-69"),sQuery(id+"F4.wireOp",EDGE,"E10.sketch_text.stroke-70"),sQuery(id+"F4.wireOp",EDGE,"E10.sketch_text.stroke-71"),sQuery(id+"F4.wireOp",EDGE,"E10.sketch_text.stroke-72"),sQuery(id+"F4.wireOp",EDGE,"E10.sketch_text.stroke-73"),sQuery(id+"F4.wireOp",EDGE,"E10.sketch_text.stroke-74"),sQuery(id+"F4.wireOp",EDGE,"E10.sketch_text.stroke-75"),sQuery(id+"F4.wireOp",EDGE,"E10.sketch_text.stroke-76"),sQuery(id+"F4.wireOp",EDGE,"E10.sketch_text.stroke-77"),sQuery(id+"F4.wireOp",EDGE,"E10.sketch_text.stroke-78"),sQuery(id+"F4.wireOp",EDGE,"E10.sketch_text.stroke-79"),sQuery(id+"F4.wireOp",EDGE,"E10.sketch_text.stroke-80"),sQuery(id+"F4.wireOp",EDGE,"E10.sketch_text.stroke-81"),sQuery(id+"F4.wireOp",EDGE,"E10.sketch_text.stroke-82"),sQuery(id+"F4.wireOp",EDGE,"E10.sketch_text.stroke-83"),sQuery(id+"F4.wireOp",EDGE,"E10.sketch_text.stroke-84"),sQuery(id+"F4.wireOp",EDGE,"E10.sketch_text.stroke-85"),sQuery(id+"F4.wireOp",EDGE,"E10.sketch_text.stroke-86"),sQuery(id+"F4.wireOp",EDGE,"E10.sketch_text.stroke-87"),sQuery(id+"F4.wireOp",EDGE,"E10.sketch_text.stroke-88"),sQuery(id+"F4.wireOp",EDGE,"E10.sketch_text.stroke-89"),sQuery(id+"F4.wireOp",EDGE,"E10.sketch_text.stroke-90"),sQuery(id+"F4.wireOp",EDGE,"E10.sketch_text.stroke-91"),sQuery(id+"F4.wireOp",EDGE,"E10.sketch_text.stroke-92"),sQuery(id+"F4.wireOp",EDGE,"E10.sketch_text.stroke-93"),sQuery(id+"F4.wireOp",EDGE,"E10.sketch_text.stroke-94"),sQuery(id+"F4.wireOp",EDGE,"E10.sketch_text.stroke-95"),sQuery(id+"F4.wireOp",EDGE,"E10.sketch_text.stroke-96"),sQuery(id+"F4.wireOp",EDGE,"E10.sketch_text.stroke-97"),sQuery(id+"F4.wireOp",EDGE,"E10.sketch_text.stroke-98"),sQuery(id+"F4.wireOp",EDGE,"E10.sketch_text.stroke-99"),sQuery(id+"F4.wireOp",EDGE,"E10.sketch_text.stroke-100"),sQuery(id+"F4.wireOp",EDGE,"E10.sketch_text.stroke-101"),sQuery(id+"F4.wireOp",EDGE,"E10.sketch_text.stroke-102"),sQuery(id+"F4.wireOp",EDGE,"E10.sketch_text.stroke-103"),sQuery(id+"F4.wireOp",EDGE,"E10.sketch_text.stroke-104")])],"isStart":false});
            var Q117;
            Q117=makeQuery(id+"F5.opExtrude","SWEPT_FACE",FACE,{"disambiguationData":[OSD([sQuery(id+"F4.wireOp",EDGE,"E10.sketch_text.stroke-33")])]});
            var Q118;
            Q118=makeQuery(id+"F5.opExtrude","SWEPT_FACE",FACE,{"disambiguationData":[OSD([sQuery(id+"F4.wireOp",EDGE,"E10.sketch_text.stroke-93")])]});
            var Q119;
            Q119=makeQuery(id+"F5.opExtrude","SWEPT_FACE",FACE,{"disambiguationData":[OSD([sQuery(id+"F4.wireOp",EDGE,"E10.sketch_text.stroke-34")])]});
            var Q120;
            Q120=makeQuery(id+"F5.opExtrude","SWEPT_FACE",FACE,{"disambiguationData":[OSD([sQuery(id+"F4.wireOp",EDGE,"E10.sketch_text.stroke-152")])]});
            var Q121;
            Q121=makeQuery(id+"F5.opExtrude","SWEPT_FACE",FACE,{"disambiguationData":[OSD([sQuery(id+"F4.wireOp",EDGE,"E10.sketch_text.stroke-51")])]});
            var Q122;
            Q122=makeQuery(id+"F5.opExtrude","SWEPT_FACE",FACE,{"disambiguationData":[OSD([sQuery(id+"F4.wireOp",EDGE,"E10.sketch_text.stroke-6")])]});
            var Q123;
            Q123=makeQuery(id+"F5.opExtrude","SWEPT_FACE",FACE,{"disambiguationData":[OSD([sQuery(id+"F4.wireOp",EDGE,"E10.sketch_text.stroke-7")])]});
            var Q124;
            Q124=makeQuery(id+"F5.opExtrude","SWEPT_FACE",FACE,{"disambiguationData":[OSD([sQuery(id+"F4.wireOp",EDGE,"E10.sketch_text.stroke-156")])]});
            var Q125;
            Q125=makeQuery(id+"F5.opExtrude","SWEPT_FACE",FACE,{"disambiguationData":[OSD([sQuery(id+"F4.wireOp",EDGE,"E10.sketch_text.stroke-112")])]});
            var Q126;
            Q126=makeQuery(id+"F5.boolean.opBoolean","SPLIT",FACE,{"disambiguationData":[TD([makeQuery(id+"F5.opExtrude","SWEPT_FACE",FACE,{"disambiguationData":[OSD([sQuery(id+"F4.wireOp",EDGE,"E10.sketch_text.stroke-182")])]})])],"derivedFrom":makeQuery(id+"F1.opExtrude","CAP_FACE",FACE,{"disambiguationData":[OSD([sQuery(id+"F0.wireOp",EDGE,"E0.bottom"),sQuery(id+"F0.wireOp",EDGE,"E0.top"),sQuery(id+"F0.wireOp",EDGE,"E0.left"),sQuery(id+"F0.wireOp",EDGE,"E0.right"),sQuery(id+"F0.wireOp",EDGE,"E1"),sQuery(id+"F0.wireOp",EDGE,"E7.MirrorC"),sQuery(id+"F0.wireOp",EDGE,"E8.MirrorC"),sQuery(id+"F0.wireOp",EDGE,"E9.MirrorC")])],"isStart":true})});
            var Q127;
            Q127=makeQuery(id+"F5.opExtrude","SWEPT_FACE",FACE,{"disambiguationData":[OSD([sQuery(id+"F4.wireOp",EDGE,"E10.sketch_text.stroke-96")])]});
            var Q128;
            Q128=makeQuery(id+"F5.opExtrude","SWEPT_FACE",FACE,{"disambiguationData":[OSD([sQuery(id+"F4.wireOp",EDGE,"E10.sketch_text.stroke-114")])]});
            var Q129;
            Q129=makeQuery(id+"F5.opExtrude","SWEPT_FACE",FACE,{"disambiguationData":[OSD([sQuery(id+"F4.wireOp",EDGE,"E10.sketch_text.stroke-39")])]});
            var Q130;
            Q130=makeQuery(id+"F5.opExtrude","SWEPT_FACE",FACE,{"disambiguationData":[OSD([sQuery(id+"F4.wireOp",EDGE,"E10.sketch_text.stroke-13")])]});
            var Q131;
            Q131=makeQuery(id+"F5.opExtrude","SWEPT_FACE",FACE,{"disambiguationData":[OSD([sQuery(id+"F4.wireOp",EDGE,"E10.sketch_text.stroke-115")])]});
            var Q132;
            Q132=makeQuery(id+"F5.opExtrude","SWEPT_FACE",FACE,{"disambiguationData":[OSD([sQuery(id+"F4.wireOp",EDGE,"E10.sketch_text.stroke-56")])]});
            var Q133;
            Q133=makeQuery(id+"F5.opExtrude","SWEPT_FACE",FACE,{"disambiguationData":[OSD([sQuery(id+"F4.wireOp",EDGE,"E10.sketch_text.stroke-144")])]});
            var Q134;
            Q134=makeQuery(id+"F5.opExtrude","SWEPT_FACE",FACE,{"disambiguationData":[OSD([sQuery(id+"F4.wireOp",EDGE,"E10.sketch_text.stroke-190")])]});
            var Q135;
            Q135=makeQuery(id+"F5.opExtrude","SWEPT_FACE",FACE,{"disambiguationData":[OSD([sQuery(id+"F4.wireOp",EDGE,"E10.sketch_text.stroke-116")])]});
            var Q136;
            Q136=makeQuery(id+"F5.opExtrude","SWEPT_FACE",FACE,{"disambiguationData":[OSD([sQuery(id+"F4.wireOp",EDGE,"E10.sketch_text.stroke-41")])]});
            var Q137;
            Q137=makeQuery(id+"F5.opExtrude","SWEPT_FACE",FACE,{"disambiguationData":[OSD([sQuery(id+"F4.wireOp",EDGE,"E10.sketch_text.stroke-161")])]});
            var Q138;
            Q138=makeQuery(id+"F5.opExtrude","SWEPT_FACE",FACE,{"disambiguationData":[OSD([sQuery(id+"F4.wireOp",EDGE,"E10.sketch_text.stroke-146")])]});
            var Q139;
            Q139=makeQuery(id+"F5.opExtrude","SWEPT_FACE",FACE,{"disambiguationData":[OSD([sQuery(id+"F4.wireOp",EDGE,"E10.sketch_text.stroke-58")])]});
            var Q140;
            Q140=makeQuery(id+"F5.opExtrude","SWEPT_FACE",FACE,{"disambiguationData":[OSD([sQuery(id+"F4.wireOp",EDGE,"E10.sketch_text.stroke-105")])]});
            var Q141;
            Q141=makeQuery(id+"F5.opExtrude","SWEPT_FACE",FACE,{"disambiguationData":[OSD([sQuery(id+"F4.wireOp",EDGE,"E10.sketch_text.stroke-177")])]});
            var Q142;
            Q142=makeQuery(id+"F5.opExtrude","SWEPT_FACE",FACE,{"disambiguationData":[OSD([sQuery(id+"F4.wireOp",EDGE,"E10.sketch_text.stroke-77")])]});
            var Q143;
            Q143=makeQuery(id+"F5.opExtrude","SWEPT_FACE",FACE,{"disambiguationData":[OSD([sQuery(id+"F4.wireOp",EDGE,"E10.sketch_text.stroke-138")])]});
            var Q144;
            Q144=makeQuery(id+"F5.opExtrude","SWEPT_FACE",FACE,{"disambiguationData":[OSD([sQuery(id+"F4.wireOp",EDGE,"E10.sketch_text.stroke-111")])]});
            var Q145;
            Q145=makeQuery(id+"F5.opExtrude","SWEPT_FACE",FACE,{"disambiguationData":[OSD([sQuery(id+"F4.wireOp",EDGE,"E10.sketch_text.stroke-53")])]});
            var Q146;
            Q146=makeQuery(id+"F5.opExtrude","SWEPT_FACE",FACE,{"disambiguationData":[OSD([sQuery(id+"F4.wireOp",EDGE,"E10.sketch_text.stroke-141")])]});
            var Q147;
            Q147=makeQuery(id+"F5.opExtrude","SWEPT_FACE",FACE,{"disambiguationData":[OSD([sQuery(id+"F4.wireOp",EDGE,"E10.sketch_text.stroke-157")])]});
            var Q148;
            Q148=makeQuery(id+"F5.opExtrude","SWEPT_FACE",FACE,{"disambiguationData":[OSD([sQuery(id+"F4.wireOp",EDGE,"E10.sketch_text.stroke-64")])]});
            var Q149;
            Q149=makeQuery(id+"F5.boolean.opBoolean","SPLIT",FACE,{"disambiguationData":[TD([makeQuery(id+"F5.opExtrude","SWEPT_FACE",FACE,{"disambiguationData":[OSD([sQuery(id+"F4.wireOp",EDGE,"E10.sketch_text.stroke-53")])]})])],"derivedFrom":makeQuery(id+"F1.opExtrude","CAP_FACE",FACE,{"disambiguationData":[OSD([sQuery(id+"F0.wireOp",EDGE,"E0.bottom"),sQuery(id+"F0.wireOp",EDGE,"E0.top"),sQuery(id+"F0.wireOp",EDGE,"E0.left"),sQuery(id+"F0.wireOp",EDGE,"E0.right"),sQuery(id+"F0.wireOp",EDGE,"E1"),sQuery(id+"F0.wireOp",EDGE,"E7.MirrorC"),sQuery(id+"F0.wireOp",EDGE,"E8.MirrorC"),sQuery(id+"F0.wireOp",EDGE,"E9.MirrorC")])],"isStart":true})});
            var Q150;
            Q150=makeQuery(id+"F5.opExtrude","SWEPT_FACE",FACE,{"disambiguationData":[OSD([sQuery(id+"F4.wireOp",EDGE,"E10.sketch_text.stroke-36")])]});
            var Q151;
            Q151=makeQuery(id+"F5.opExtrude","SWEPT_FACE",FACE,{"disambiguationData":[OSD([sQuery(id+"F4.wireOp",EDGE,"E10.sketch_text.stroke-22")])]});
            var Q152;
            Q152=makeQuery(id+"F5.boolean.opBoolean","SPLIT",FACE,{"disambiguationData":[TD([makeQuery(id+"F5.opExtrude","SWEPT_FACE",FACE,{"disambiguationData":[OSD([sQuery(id+"F4.wireOp",EDGE,"E10.sketch_text.stroke-119")])]})])],"derivedFrom":makeQuery(id+"F1.opExtrude","CAP_FACE",FACE,{"disambiguationData":[OSD([sQuery(id+"F0.wireOp",EDGE,"E0.bottom"),sQuery(id+"F0.wireOp",EDGE,"E0.top"),sQuery(id+"F0.wireOp",EDGE,"E0.left"),sQuery(id+"F0.wireOp",EDGE,"E0.right"),sQuery(id+"F0.wireOp",EDGE,"E1"),sQuery(id+"F0.wireOp",EDGE,"E7.MirrorC"),sQuery(id+"F0.wireOp",EDGE,"E8.MirrorC"),sQuery(id+"F0.wireOp",EDGE,"E9.MirrorC")])],"isStart":true})});
            var Q153;
            Q153=makeQuery(id+"F5.boolean.opBoolean","SPLIT",FACE,{"disambiguationData":[TD([makeQuery(id+"F5.opExtrude","SWEPT_FACE",FACE,{"disambiguationData":[OSD([sQuery(id+"F4.wireOp",EDGE,"E10.sketch_text.stroke-158")])]})])],"derivedFrom":makeQuery(id+"F1.opExtrude","CAP_FACE",FACE,{"disambiguationData":[OSD([sQuery(id+"F0.wireOp",EDGE,"E0.bottom"),sQuery(id+"F0.wireOp",EDGE,"E0.top"),sQuery(id+"F0.wireOp",EDGE,"E0.left"),sQuery(id+"F0.wireOp",EDGE,"E0.right"),sQuery(id+"F0.wireOp",EDGE,"E1"),sQuery(id+"F0.wireOp",EDGE,"E7.MirrorC"),sQuery(id+"F0.wireOp",EDGE,"E8.MirrorC"),sQuery(id+"F0.wireOp",EDGE,"E9.MirrorC")])],"isStart":true})});
            var Q154;
            Q154=makeQuery(id+"F5.opExtrude","SWEPT_FACE",FACE,{"disambiguationData":[OSD([sQuery(id+"F4.wireOp",EDGE,"E10.sketch_text.stroke-9")])]});
            var Q155;
            Q155=makeQuery(id+"F5.opExtrude","SWEPT_FACE",FACE,{"disambiguationData":[OSD([sQuery(id+"F4.wireOp",EDGE,"E10.sketch_text.stroke-167")])]});
            var Q156;
            Q156=makeQuery(id+"F5.opExtrude","SWEPT_FACE",FACE,{"disambiguationData":[OSD([sQuery(id+"F4.wireOp",EDGE,"E10.sketch_text.stroke-95")])]});
            var Q157;
            Q157=makeQuery(id+"F5.opExtrude","SWEPT_FACE",FACE,{"disambiguationData":[OSD([sQuery(id+"F4.wireOp",EDGE,"E10.sketch_text.stroke-184")])]});
            var Q158;
            Q158=makeQuery(id+"F5.opExtrude","SWEPT_FACE",FACE,{"disambiguationData":[OSD([sQuery(id+"F4.wireOp",EDGE,"E10.sketch_text.stroke-84")])]});
            var Q159;
            Q159=makeQuery(id+"F5.opExtrude","SWEPT_FACE",FACE,{"disambiguationData":[OSD([sQuery(id+"F4.wireOp",EDGE,"E10.sketch_text.stroke-68")])]});
            var Q160;
            Q160=makeQuery(id+"F5.opExtrude","SWEPT_FACE",FACE,{"disambiguationData":[OSD([sQuery(id+"F4.wireOp",EDGE,"E10.sketch_text.stroke-143")])]});
            var Q161;
            Q161=makeQuery(id+"F5.opExtrude","SWEPT_FACE",FACE,{"disambiguationData":[OSD([sQuery(id+"F4.wireOp",EDGE,"E10.sketch_text.stroke-189")])]});
            var Q162;
            Q162=makeQuery(id+"F5.opExtrude","CAP_FACE",FACE,{"disambiguationData":[OSD([sQuery(id+"F4.wireOp",EDGE,"E10.sketch_text.stroke-13"),sQuery(id+"F4.wireOp",EDGE,"E10.sketch_text.stroke-14"),sQuery(id+"F4.wireOp",EDGE,"E10.sketch_text.stroke-15"),sQuery(id+"F4.wireOp",EDGE,"E10.sketch_text.stroke-16"),sQuery(id+"F4.wireOp",EDGE,"E10.sketch_text.stroke-17"),sQuery(id+"F4.wireOp",EDGE,"E10.sketch_text.stroke-18"),sQuery(id+"F4.wireOp",EDGE,"E10.sketch_text.stroke-19"),sQuery(id+"F4.wireOp",EDGE,"E10.sketch_text.stroke-20")])],"isStart":false});
            var Q163;
            Q163=makeQuery(id+"F5.opExtrude","SWEPT_FACE",FACE,{"disambiguationData":[OSD([sQuery(id+"F4.wireOp",EDGE,"E10.sketch_text.stroke-57")])]});
            var Q164;
            Q164=makeQuery(id+"F5.opExtrude","SWEPT_FACE",FACE,{"disambiguationData":[OSD([sQuery(id+"F4.wireOp",EDGE,"E10.sketch_text.stroke-29")])]});
            var Q165;
            Q165=makeQuery(id+"F5.opExtrude","SWEPT_FACE",FACE,{"disambiguationData":[OSD([sQuery(id+"F4.wireOp",EDGE,"E10.sketch_text.stroke-60")])]});
            var Q166;
            Q166=makeQuery(id+"F5.opExtrude","SWEPT_FACE",FACE,{"disambiguationData":[OSD([sQuery(id+"F4.wireOp",EDGE,"E10.sketch_text.stroke-148")])]});
            var Q167;
            Q167=makeQuery(id+"F5.opExtrude","SWEPT_FACE",FACE,{"disambiguationData":[OSD([sQuery(id+"F4.wireOp",EDGE,"E10.sketch_text.stroke-75")])]});
            var Q168;
            Q168=makeQuery(id+"F5.opExtrude","SWEPT_FACE",FACE,{"disambiguationData":[OSD([sQuery(id+"F4.wireOp",EDGE,"E10.sketch_text.stroke-91")])]});
            var Q169;
            Q169=makeQuery(id+"F5.opExtrude","SWEPT_FACE",FACE,{"disambiguationData":[OSD([sQuery(id+"F4.wireOp",EDGE,"E10.sketch_text.stroke-78")])]});
            var Q170;
            Q170=makeQuery(id+"F5.opExtrude","SWEPT_FACE",FACE,{"disambiguationData":[OSD([sQuery(id+"F4.wireOp",EDGE,"E10.sketch_text.stroke-62")])]});
            var Q171;
            Q171=makeQuery(id+"F5.opExtrude","SWEPT_FACE",FACE,{"disambiguationData":[OSD([sQuery(id+"F4.wireOp",EDGE,"E10.sketch_text.stroke-182")])]});
            var Q172;
            Q172=makeQuery(id+"F5.opExtrude","SWEPT_FACE",FACE,{"disambiguationData":[OSD([sQuery(id+"F4.wireOp",EDGE,"E10.sketch_text.stroke-11")])]});
            var Q173;
            Q173=makeQuery(id+"F5.opExtrude","SWEPT_FACE",FACE,{"disambiguationData":[OSD([sQuery(id+"F4.wireOp",EDGE,"E10.sketch_text.stroke-97")])]});
            var Q174;
            Q174=makeQuery(id+"F5.opExtrude","SWEPT_FACE",FACE,{"disambiguationData":[OSD([sQuery(id+"F4.wireOp",EDGE,"E10.sketch_text.stroke-23")])]});
            var Q175;
            Q175=makeQuery(id+"F5.opExtrude","SWEPT_FACE",FACE,{"disambiguationData":[OSD([sQuery(id+"F4.wireOp",EDGE,"E10.sketch_text.stroke-80")])]});
            var Q176;
            Q176=makeQuery(id+"F5.boolean.opBoolean","SPLIT",FACE,{"disambiguationData":[TD([makeQuery(id+"F5.opExtrude","SWEPT_FACE",FACE,{"disambiguationData":[OSD([sQuery(id+"F4.wireOp",EDGE,"E10.sketch_text.stroke-99")])]})])],"derivedFrom":makeQuery(id+"F1.opExtrude","CAP_FACE",FACE,{"disambiguationData":[OSD([sQuery(id+"F0.wireOp",EDGE,"E0.bottom"),sQuery(id+"F0.wireOp",EDGE,"E0.top"),sQuery(id+"F0.wireOp",EDGE,"E0.left"),sQuery(id+"F0.wireOp",EDGE,"E0.right"),sQuery(id+"F0.wireOp",EDGE,"E1"),sQuery(id+"F0.wireOp",EDGE,"E7.MirrorC"),sQuery(id+"F0.wireOp",EDGE,"E8.MirrorC"),sQuery(id+"F0.wireOp",EDGE,"E9.MirrorC")])],"isStart":true})});
            var Q177;
            Q177=makeQuery(id+"F5.opExtrude","SWEPT_FACE",FACE,{"disambiguationData":[OSD([sQuery(id+"F4.wireOp",EDGE,"E10.sketch_text.stroke-168")])]});
            var Q178;
            Q178=makeQuery(id+"F5.opExtrude","SWEPT_FACE",FACE,{"disambiguationData":[OSD([sQuery(id+"F4.wireOp",EDGE,"E10.sketch_text.stroke-188")])]});
            var Q179;
            Q179=makeQuery(id+"F5.opExtrude","SWEPT_FACE",FACE,{"disambiguationData":[OSD([sQuery(id+"F4.wireOp",EDGE,"E10.sketch_text.stroke-129")])]});
            var Q180;
            Q180=makeQuery(id+"F5.opExtrude","SWEPT_FACE",FACE,{"disambiguationData":[OSD([sQuery(id+"F4.wireOp",EDGE,"E10.sketch_text.stroke-27")])]});
            var Q181;
            Q181=makeQuery(id+"F5.opExtrude","SWEPT_FACE",FACE,{"disambiguationData":[OSD([sQuery(id+"F4.wireOp",EDGE,"E10.sketch_text.stroke-175")])]});
            var Q182;
            Q182=makeQuery(id+"F5.opExtrude","SWEPT_FACE",FACE,{"disambiguationData":[OSD([sQuery(id+"F4.wireOp",EDGE,"E10.sketch_text.stroke-42")])]});
            var Q183;
            Q183=makeQuery(id+"F5.opExtrude","SWEPT_FACE",FACE,{"disambiguationData":[OSD([sQuery(id+"F4.wireOp",EDGE,"E10.sketch_text.stroke-118")])]});
            var Q184;
            Q184=makeQuery(id+"F5.opExtrude","SWEPT_FACE",FACE,{"disambiguationData":[OSD([sQuery(id+"F4.wireOp",EDGE,"E10.sketch_text.stroke-151")])]});
            var Q185;
            Q185=makeQuery(id+"F5.opExtrude","SWEPT_FACE",FACE,{"disambiguationData":[OSD([sQuery(id+"F4.wireOp",EDGE,"E10.sketch_text.stroke-137")])]});
            var Q186;
            Q186=makeQuery(id+"F5.opExtrude","SWEPT_FACE",FACE,{"disambiguationData":[OSD([sQuery(id+"F4.wireOp",EDGE,"E10.sketch_text.stroke-83")])]});
            var Q187;
            Q187=makeQuery(id+"F5.boolean.opBoolean","SPLIT",FACE,{"disambiguationData":[TD([makeQuery(id+"F5.opExtrude","SWEPT_FACE",FACE,{"disambiguationData":[OSD([sQuery(id+"F4.wireOp",EDGE,"E10.sketch_text.stroke-90")])]})])],"derivedFrom":makeQuery(id+"F1.opExtrude","CAP_FACE",FACE,{"disambiguationData":[OSD([sQuery(id+"F0.wireOp",EDGE,"E0.bottom"),sQuery(id+"F0.wireOp",EDGE,"E0.top"),sQuery(id+"F0.wireOp",EDGE,"E0.left"),sQuery(id+"F0.wireOp",EDGE,"E0.right"),sQuery(id+"F0.wireOp",EDGE,"E1"),sQuery(id+"F0.wireOp",EDGE,"E7.MirrorC"),sQuery(id+"F0.wireOp",EDGE,"E8.MirrorC"),sQuery(id+"F0.wireOp",EDGE,"E9.MirrorC")])],"isStart":true})});
            var Q188;
            Q188=makeQuery(id+"F5.opExtrude","SWEPT_FACE",FACE,{"disambiguationData":[OSD([sQuery(id+"F4.wireOp",EDGE,"E10.sketch_text.stroke-139")])]});
            var Q189;
            Q189=makeQuery(id+"F5.opExtrude","SWEPT_FACE",FACE,{"disambiguationData":[OSD([sQuery(id+"F4.wireOp",EDGE,"E10.sketch_text.stroke-70")])]});
            var Q190;
            Q190=makeQuery(id+"F5.opExtrude","SWEPT_FACE",FACE,{"disambiguationData":[OSD([sQuery(id+"F4.wireOp",EDGE,"E10.sketch_text.stroke-160")])]});
            var Q191;
            Q191=makeQuery(id+"F5.opExtrude","SWEPT_FACE",FACE,{"disambiguationData":[OSD([sQuery(id+"F4.wireOp",EDGE,"E10.sketch_text.stroke-71")])]});
            var Q192;
            Q192=makeQuery(id+"F5.opExtrude","SWEPT_FACE",FACE,{"disambiguationData":[OSD([sQuery(id+"F4.wireOp",EDGE,"E10.sketch_text.stroke-117")])]});
            var Q193;
            Q193=makeQuery(id+"F5.opExtrude","SWEPT_FACE",FACE,{"disambiguationData":[OSD([sQuery(id+"F4.wireOp",EDGE,"E10.sketch_text.stroke-147")])]});
            var Q194;
            Q194=makeQuery(id+"F5.opExtrude","SWEPT_FACE",FACE,{"disambiguationData":[OSD([sQuery(id+"F4.wireOp",EDGE,"E10.sketch_text.stroke-164")])]});
            var Q195;
            Q195=makeQuery(id+"F5.opExtrude","SWEPT_FACE",FACE,{"disambiguationData":[OSD([sQuery(id+"F4.wireOp",EDGE,"E10.sketch_text.stroke-61")])]});
            var Q196;
            Q196=makeQuery(id+"F5.opExtrude","SWEPT_FACE",FACE,{"disambiguationData":[OSD([sQuery(id+"F4.wireOp",EDGE,"E10.sketch_text.stroke-19")])]});
            var Q197;
            Q197=makeQuery(id+"F5.opExtrude","SWEPT_FACE",FACE,{"disambiguationData":[OSD([sQuery(id+"F4.wireOp",EDGE,"E10.sketch_text.stroke-35")])]});
            var Q198;
            Q198=makeQuery(id+"F5.opExtrude","SWEPT_FACE",FACE,{"disambiguationData":[OSD([sQuery(id+"F4.wireOp",EDGE,"E10.sketch_text.stroke-140")])]});
            var Q199;
            Q199=makeQuery(id+"F5.opExtrude","SWEPT_FACE",FACE,{"disambiguationData":[OSD([sQuery(id+"F4.wireOp",EDGE,"E10.sketch_text.stroke-20")])]});
            var Q200;
            Q200=makeQuery(id+"F5.opExtrude","SWEPT_FACE",FACE,{"disambiguationData":[OSD([sQuery(id+"F4.wireOp",EDGE,"E10.sketch_text.stroke-16")])]});
            var Q201;
            Q201=makeQuery(id+"F5.opExtrude","SWEPT_FACE",FACE,{"disambiguationData":[OSD([sQuery(id+"F4.wireOp",EDGE,"E10.sketch_text.stroke-18")])]});
            var Q202;
            Q202=makeQuery(id+"F5.opExtrude","SWEPT_FACE",FACE,{"disambiguationData":[OSD([sQuery(id+"F4.wireOp",EDGE,"E10.sketch_text.stroke-17")])]});
            var Q203;
            Q203=qCreatedBy(makeId("Right.planeOp"),FACE);
            mirror(context, id + "F6", {"operationType" : NewBodyOperationType.ADD, "entities" : qUnion([Q0]), "faces" : qUnion([Q1, Q2, Q3, Q4, Q5, Q6, Q7, Q8, Q9, Q10, Q11, Q12, Q13, Q14, Q15, Q16, Q17, Q18, Q19, Q20, Q21, Q22, Q23, Q24, Q25, Q26, Q27, Q28, Q29, Q30, Q31, Q32, Q33, Q34, Q35, Q36, Q37, Q38, Q39, Q40, Q41, Q42, Q43, Q44, Q45, Q46, Q47, Q48, Q49, Q50, Q51, Q52, Q53, Q54, Q55, Q56, Q57, Q58, Q59, Q60, Q61, Q62, Q63, Q64, Q65, Q66, Q67, Q68, Q69, Q70, Q71, Q72, Q73, Q74, Q75, Q76, Q77, Q78, Q79, Q80, Q81, Q82, Q83, Q84, Q85, Q86, Q87, Q88, Q89, Q90, Q91, Q92, Q93, Q94, Q95, Q96, Q97, Q98, Q99, Q100, Q101, Q102, Q103, Q104, Q105, Q106, Q107, Q108, Q109, Q110, Q111, Q112, Q113, Q114, Q115, Q116, Q117, Q118, Q119, Q120, Q121, Q122, Q123, Q124, Q125, Q126, Q127, Q128, Q129, Q130, Q131, Q132, Q133, Q134, Q135, Q136, Q137, Q138, Q139, Q140, Q141, Q142, Q143, Q144, Q145, Q146, Q147, Q148, Q149, Q150, Q151, Q152, Q153, Q154, Q155, Q156, Q157, Q158, Q159, Q160, Q161, Q162, Q163, Q164, Q165, Q166, Q167, Q168, Q169, Q170, Q171, Q172, Q173, Q174, Q175, Q176, Q177, Q178, Q179, Q180, Q181, Q182, Q183, Q184, Q185, Q186, Q187, Q188, Q189, Q190, Q191, Q192, Q193, Q194, Q195, Q196, Q197, Q198, Q199, Q200, Q201, Q202]), "mirrorPlane" : qUnion([Q203])});
        }
    });
